# Revit family: Faucet-Lavatory-Grohe-Plus-20302_Series
name_source: partatom
category: Plumbing Fixtures
units: mm (PartAtom-declared; Revit-internal decimal feet)

## family parameters
Always vertical = No
Cut with Voids When Loaded = No
OmniClass Number = 23.45.55.17
OmniClass Title = Mixing Faucets
Part Type = Normal
Room Calculation Point = No
Round Connector Dimension = Use Diameter
Shared = Yes
Work Plane-Based = Yes

## types (2) — shared parameters
ADA Compliant = Yes
Assembly Code = D2020300
CW Connection = Yes
CWFU = 1.5
CalGreen Compliant = Yes
Cold Water Connection Diameter = 3/8"
Cold Water Connection Radius = 3/16"
Default Elevation = 0"
Description = Plus 8-Inch Widespread 2-Hnadle L-Size Bathroom Faucet 1.2GPM
Flow Rate = 1.2 gpm (4.56 L/min)
HW Connection = Yes
HWFU = 1.5
Height = 6 7/8"
Hot Water Connection Diameter = 0"
Hot Water Connection Radius = 3/16"
Installation Instruction Link = https://americanstandard.box.com
Installation Type = Deck-Mounted
Length = 8"
Manufacturer = Grohe
Price = Prices may vary. Please consult Manufacturer Representative for most up-to-date price list.
Product Documentation Link = https://americanstandard.box.com
Product Page URL = https://www.grohe.us
Revised Date = 03/30/2021
Type Comments = Metal lever handle, 1/2" (13mm) ceramic cartridge (90° turn), GROHE StarLight chrome finish, GROHE EcoJoy, GROHE AquaGuide adjustable flow control, GROHE QuickFix rapid installation system, Spout with flow control, Includes waste-set drain assembly, Pressure resistant flexible connection hoses (between spout and side valves), Max flow rate: 4.56 L/min (1.2 gpm)
URL = http://www.grohe.com
Vent Connection = No
WFU = 2
Warranty Documentation Link = https://cdn.cloud.grohe.com
Waste Connection = No
Width = 5 1/16"
cUPC Compliant = Yes

## per-type parameters (varying)
| type | Finish | Material | Shipping Weight |
| 20302003 | Metal-Grohe-003-StarLight Chrome | Metal-Grohe-003-StarLight Chrome | 8.40 lb |
| 20302EN3 | Metal-Grohe-EN3-Brushed Nickel Infinity Finish | Metal-Grohe-EN3-Brushed Nickel Infinity Finish | 5.86 lb |

note: column(s) folded — value = type name in every type: Model

## geometry (parser evidence)
native form markers: Sweep x2
no freeform markers — native parametric forms only
